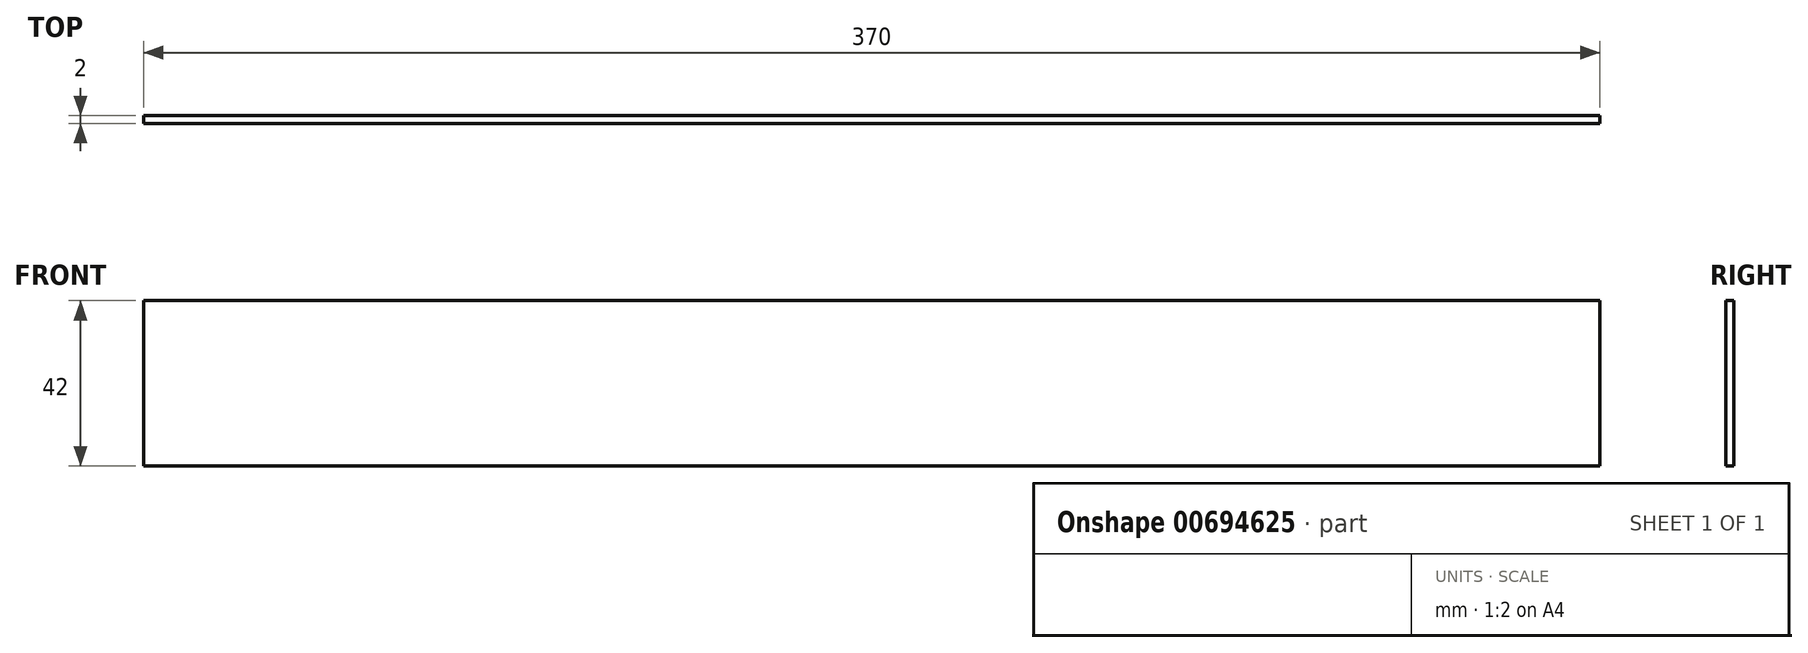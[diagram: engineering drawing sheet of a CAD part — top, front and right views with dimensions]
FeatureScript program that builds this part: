
annotation { "Feature Type Name" : "Feature", "Feature Type Description" : "" }
export const myFeature = defineFeature(function(context is Context, id is Id, definition is map)
    precondition{}
    {
        {
            var Q0;
            Q0=qCreatedBy(makeId("Front.planeOp"),FACE);
            var sketch = newSketch(context, id + "F0", { "sketchPlane" : qUnion([Q0])});
            skLineSegment(sketch, "E0.bottom", {"start": v(185, 21) * mm, "end": v(-185, 21) * mm});
            skLineSegment(sketch, "E0.top", {"start": v(185, -21) * mm, "end": v(-185, -21) * mm});
            skLineSegment(sketch, "E0.left", {"start": v(185, 21) * mm, "end": v(185, -21) * mm});
            skLineSegment(sketch, "E0.right", {"start": v(-185, 21) * mm, "end": v(-185, -21) * mm});
            skPoint(sketch, "E0.middle", {"position": v(0, 0) * mm});
            skSolve(sketch);
        }
        {
            var Q0;
            Q0=qSketchRegion(id+"F0",true);
            extrude(context, id + "F1", {"entities" : qUnion([Q0]), "depth" : 2 * mm, "offsetDistance" : 25 * mm});
        }
    });
